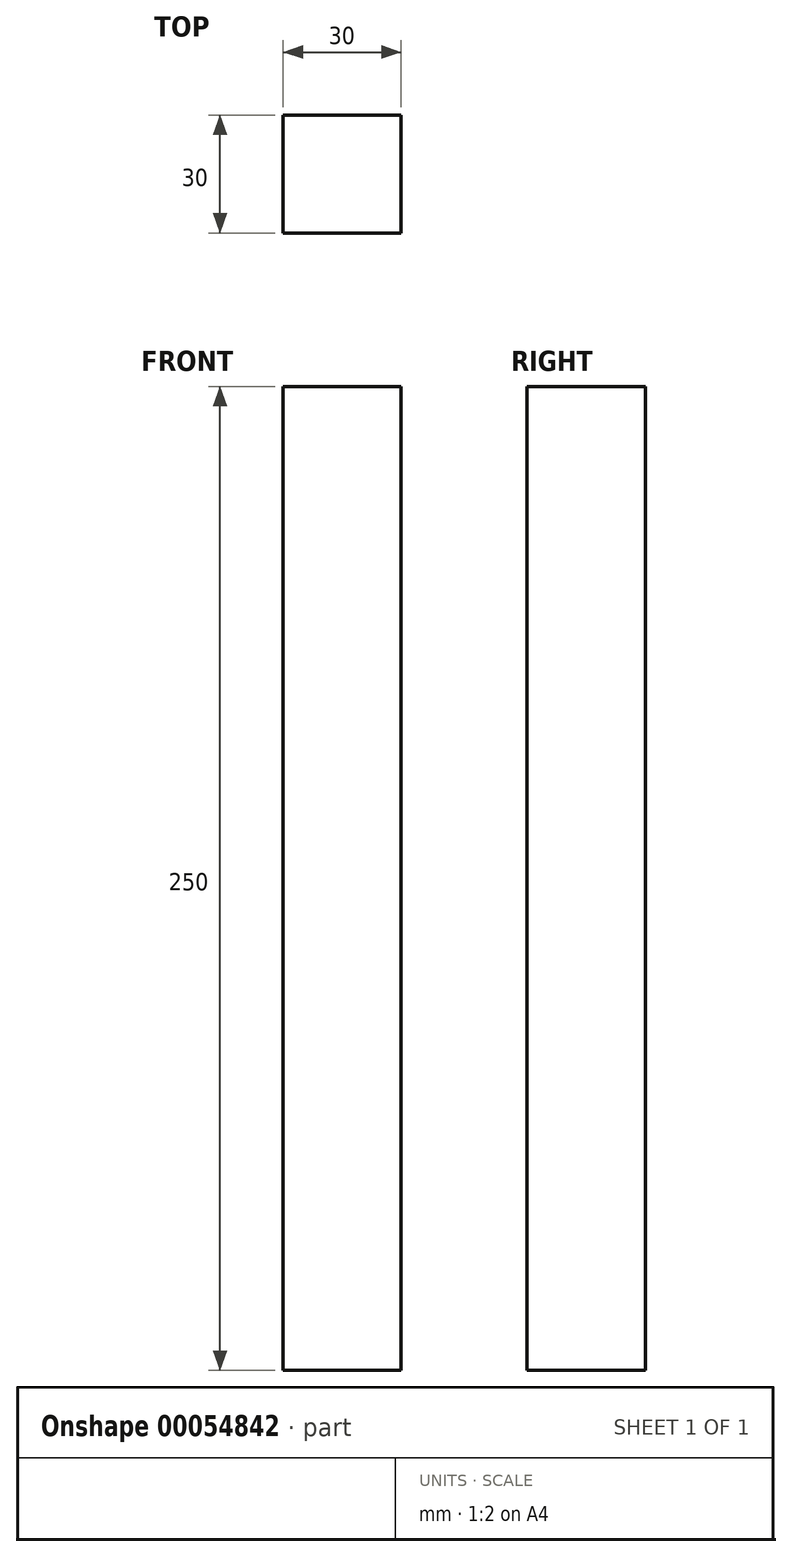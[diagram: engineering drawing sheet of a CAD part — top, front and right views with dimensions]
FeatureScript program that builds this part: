
annotation { "Feature Type Name" : "Feature", "Feature Type Description" : "" }
export const myFeature = defineFeature(function(context is Context, id is Id, definition is map)
    precondition{}
    {
        {
            var Q0;
            Q0=qCreatedBy(makeId("Top.planeOp"),FACE);
            var sketch = newSketch(context, id + "F0", { "sketchPlane" : qUnion([Q0])});
            skLineSegment(sketch, "E0.bottom", {"start": v(-52.22, -2.11) * mm, "end": v(-22.22, -2.11) * mm});
            skLineSegment(sketch, "E0.top", {"start": v(-52.22, -32.11) * mm, "end": v(-22.22, -32.11) * mm});
            skLineSegment(sketch, "E0.left", {"start": v(-52.22, -2.11) * mm, "end": v(-52.22, -32.11) * mm});
            skLineSegment(sketch, "E0.right", {"start": v(-22.22, -2.11) * mm, "end": v(-22.22, -32.11) * mm});
            skSolve(sketch);
        }
        {
            var Q0;
            Q0=makeQuery(id+"F0.imprint","IMPRINT",FACE,{"disambiguationData":[TD([[makeQuery(id+"F0.imprint","IMPRINT",EDGE,{"derivedFrom":sQuery(id+"F0.wireOp",EDGE,"E0.bottom")}),-1.0]])]});
            extrude(context, id + "F1", {"entities" : qUnion([Q0]), "depth" : 250 * mm});
        }
    });
